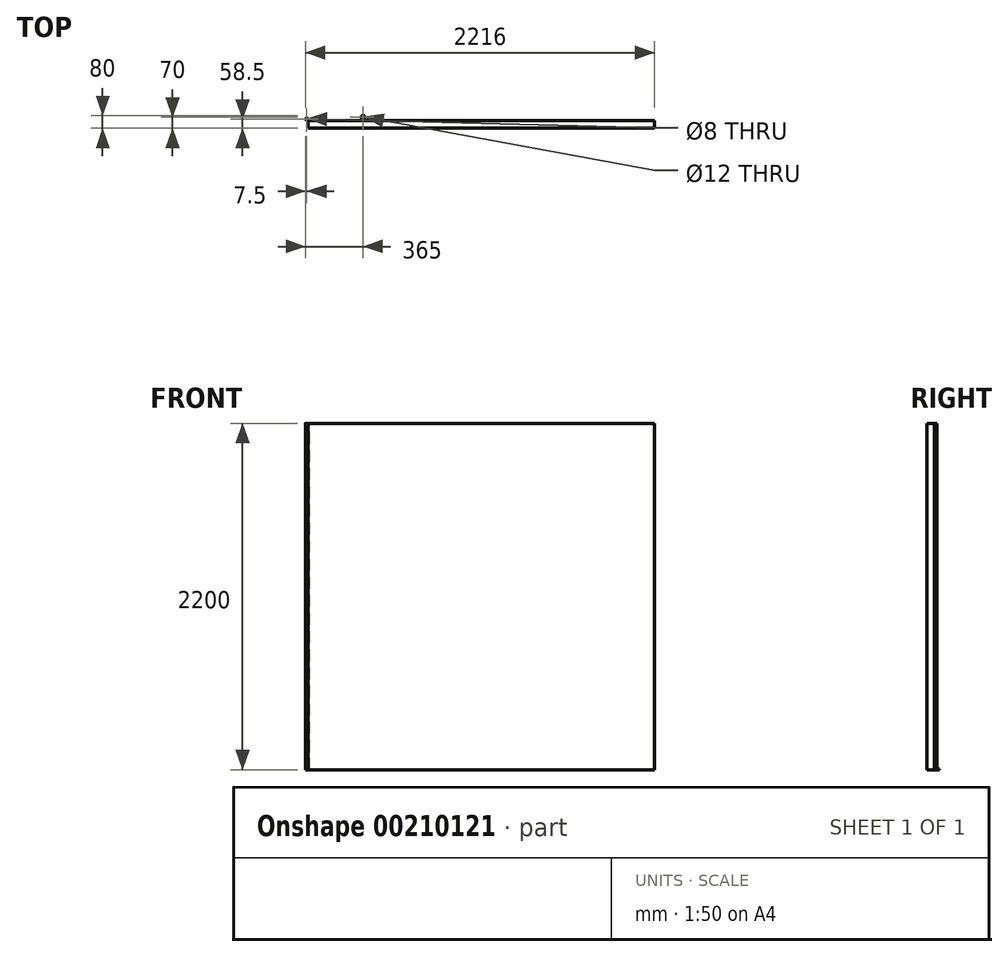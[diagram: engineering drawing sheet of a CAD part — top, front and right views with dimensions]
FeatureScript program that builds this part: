
annotation { "Feature Type Name" : "Feature", "Feature Type Description" : "" }
export const myFeature = defineFeature(function(context is Context, id is Id, definition is map)
    precondition{}
    {
        {
            var Q0;
            Q0=qCreatedBy(makeId("Front.planeOp"),FACE);
            var sketch = newSketch(context, id + "F0", { "sketchPlane" : qUnion([Q0])});
            skLineSegment(sketch, "E0.bottom", {"start": v(-1100, 1100) * mm, "end": v(1100, 1100) * mm});
            skLineSegment(sketch, "E0.top", {"start": v(-1100, -1100) * mm, "end": v(1100, -1100) * mm});
            skLineSegment(sketch, "E0.left", {"start": v(-1100, 1100) * mm, "end": v(-1100, -1100) * mm});
            skLineSegment(sketch, "E0.right", {"start": v(1100, 1100) * mm, "end": v(1100, -1100) * mm});
            skPoint(sketch, "E0.middle", {"position": v(0, 0) * mm});
            skSolve(sketch);
        }
        {
            var Q0;
            Q0 = qSketchRegion(id + "F0", true);
            extrude(context, id + "F1", {"entities" : qUnion([Q0]), "depth" : 50 * mm});
        }
        {
            var Q0;
            Q0=makeQuery(id+"F1.opExtrude","SWEPT_FACE",FACE,{"disambiguationData":[OSD([sQuery(id+"F0.wireOp",EDGE,"E0.bottom")])]});
            var sketch = newSketch(context, id + "F2", { "sketchPlane" : qUnion([Q0])});
            skCircle(sketch, "E1", {"center": v(-1108.5, 8.5) * mm, "radius": 7.5 * mm});
            skCircle(sketch, "E2", {"center": v(-1108.5, 8.5) * mm, "radius": 4 * mm});
            skLineSegment(sketch, "E3", {"start": v(-1100, 0) * mm, "end": v(-1108.46, 0) * mm});
            skLineSegment(sketch, "E4", {"start": v(-1108.46, 0) * mm, "end": v(-1108.46, 1) * mm});
            skLineSegment(sketch, "E5", {"start": v(-1100, 0) * mm, "end": v(-1090.03, 0) * mm});
            skLineSegment(sketch, "E6", {"start": v(-1090.03, 0) * mm, "end": v(-1090.03, 1.7) * mm});
            skLineSegment(sketch, "E7", {"start": v(-1090.03, 1.7) * mm, "end": v(-1105.35, 1.7) * mm});
            skSolve(sketch);
        }
        {
            var Q0;
            Q0 = qSketchRegion(id + "F2", true);
            extrude(context, id + "F3", {"entities" : qUnion([Q0]), "operationType" : NewBodyOperationType.ADD, "oppositeDirection" : true, "depth" : 2200 * mm});
        }
        {
            var Q0;
            Q0=makeQuery(id+"F3.boolean.opBoolean","MERGE",FACE,{"derivedFrom":[makeQuery(id+"F1.opExtrude","SWEPT_FACE",FACE,{"disambiguationData":[OSD([sQuery(id+"F0.wireOp",EDGE,"E0.top")])]}),makeQuery(id+"F3.opExtrude","CAP_FACE",FACE,{"disambiguationData":[OSD([sQuery(id+"F2.wireOp",EDGE,"E1"),sQuery(id+"F2.wireOp",EDGE,"E2"),sQuery(id+"F2.wireOp",EDGE,"E3"),sQuery(id+"F2.wireOp",EDGE,"E4"),sQuery(id+"F2.wireOp",EDGE,"E5"),sQuery(id+"F2.wireOp",EDGE,"E6"),sQuery(id+"F2.wireOp",EDGE,"E7")])],"isStart":false})]});
            var sketch = newSketch(context, id + "F4", { "sketchPlane" : qUnion([Q0])});
            skLineSegment(sketch, "E8.bottom", {"start": v(-761, 0) * mm, "end": v(-741, 0) * mm});
            skLineSegment(sketch, "E8.top", {"start": v(-761, -30) * mm, "end": v(-741, -30) * mm});
            skLineSegment(sketch, "E8.left", {"start": v(-761, 0) * mm, "end": v(-761, -30) * mm});
            skLineSegment(sketch, "E8.right", {"start": v(-741, 0) * mm, "end": v(-741, -30) * mm});
            skCircle(sketch, "E9", {"center": v(-751, -20) * mm, "radius": 6 * mm});
            skLineSegment(sketch, "E10", {"start": v(-751, -20) * mm, "end": v(-751, -30) * mm, "construction": true});
            skSolve(sketch);
        }
        {
            var Q0;
            Q0 = qSketchRegion(id + "F4", true);
            extrude(context, id + "F5", {"entities" : qUnion([Q0]), "operationType" : NewBodyOperationType.ADD, "oppositeDirection" : true, "depth" : 5 * mm});
        }
    });
